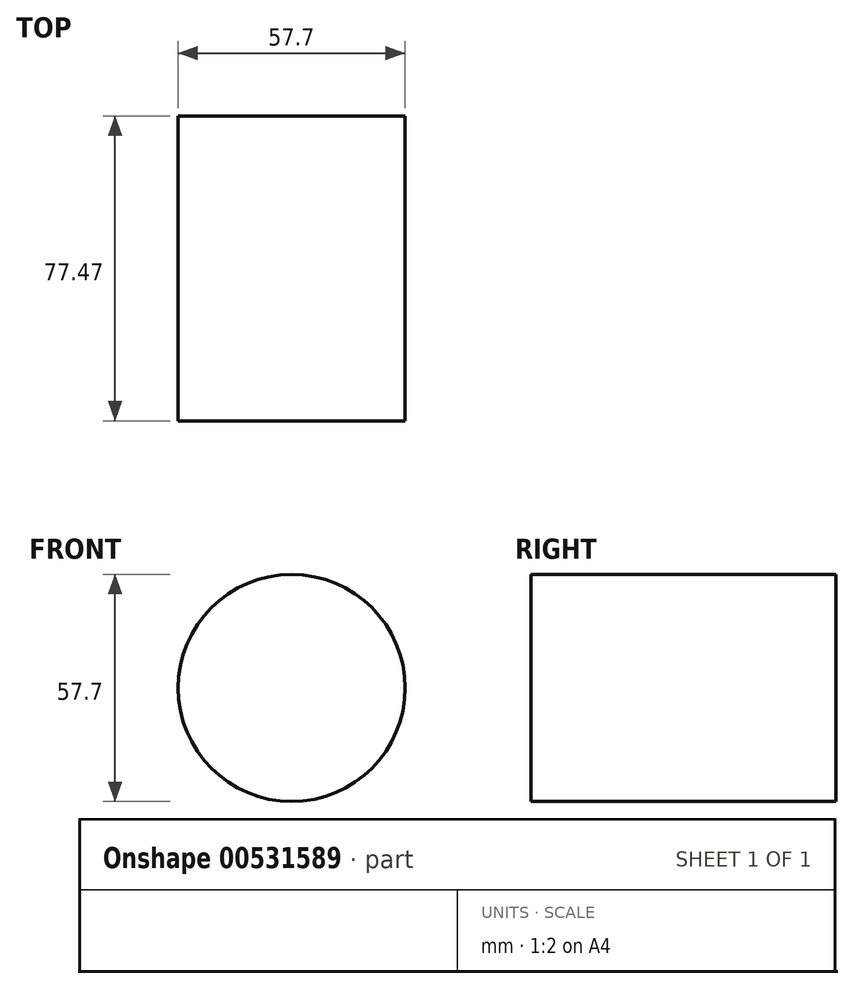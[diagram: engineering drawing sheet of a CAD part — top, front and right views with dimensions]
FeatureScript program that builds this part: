
annotation { "Feature Type Name" : "Feature", "Feature Type Description" : "" }
export const myFeature = defineFeature(function(context is Context, id is Id, definition is map)
    precondition{}
    {
        {
            var Q0;
            Q0=qCreatedBy(makeId("Front.planeOp"),FACE);
            var sketch = newSketch(context, id + "F0", { "sketchPlane" : qUnion([Q0])});
            skCircle(sketch, "E0", {"center": v(0, 0) * mm, "radius": 28.85 * mm});
            skSolve(sketch);
        }
        {
            var Q0;
            Q0=makeQuery(id+"F0.imprint","IMPRINT",FACE,{"disambiguationData":[TD([[makeQuery(id+"F0.imprint","IMPRINT",EDGE,{"derivedFrom":sQuery(id+"F0.wireOp",EDGE,"E0")}),1.0]])]});
            extrude(context, id + "F1", {"entities" : qUnion([Q0]), "depth" : 77.47 * mm, "offsetDistance" : 25.4 * mm});
        }
    });
